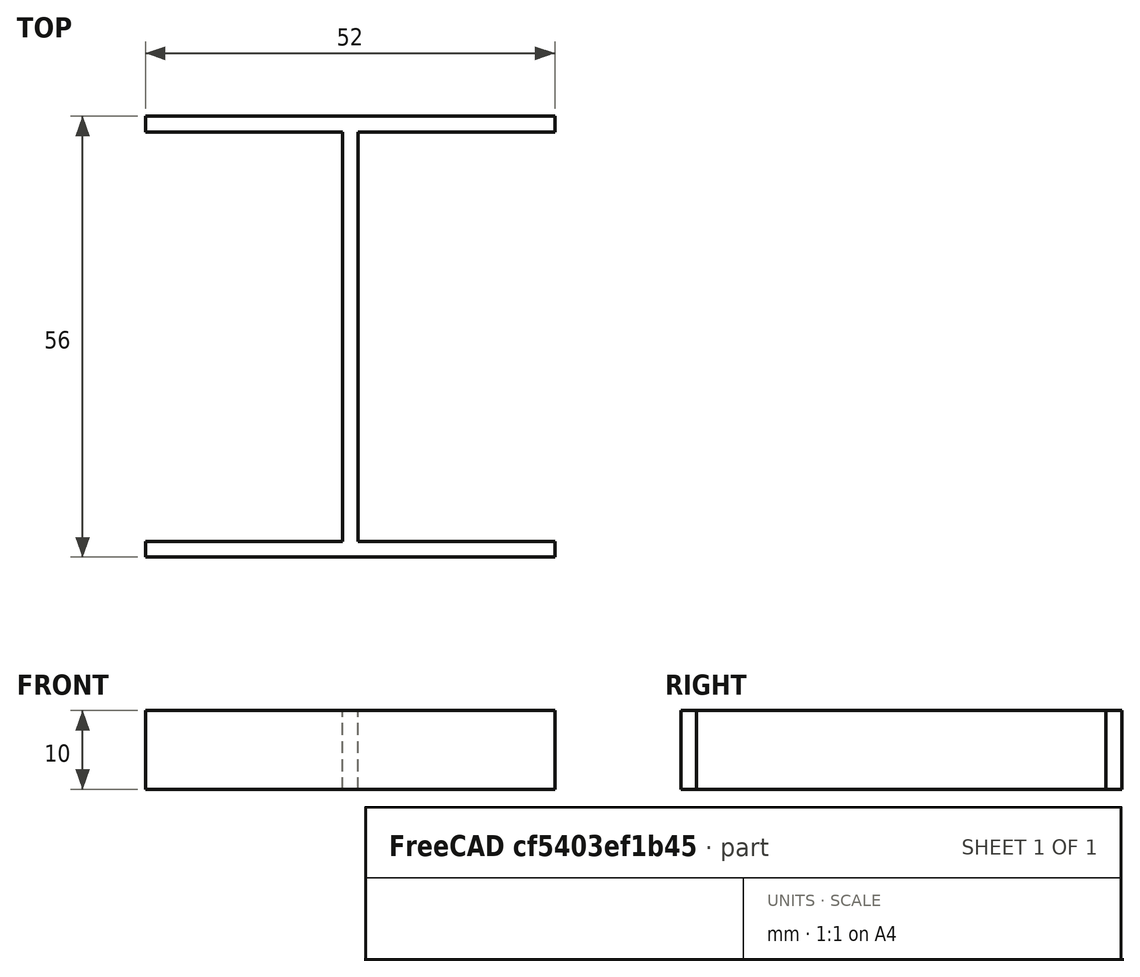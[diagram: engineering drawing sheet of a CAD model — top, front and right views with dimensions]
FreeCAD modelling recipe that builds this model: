
FCSTD DOCUMENT  (FreeCAD 1.0R38806 (Git))
Label: BedBracket
License: All rights reserved
LicenseURL: https://en.wikipedia.org/wiki/All_rights_reserved
objects: Sketcher::SketchObject×1, PartDesign::Pad×1, PartDesign::Body×1
note: 6 computed .brp shape members not serialized (recipe doc carries the construction recipe); baked Part::Feature solids carry a one-line shape summary decoded from their .brp

FEATURE [Sketcher::SketchObject] Sketch
  ArcFitTolerance = 1e-06
  AttachmentSupport = -> [XY_Plane]
  FullyConstrained = true
  MakeInternals = false
  MapMode = 5
  sketch-geometry (12):
    g0: LineSegment StartX=25 StartY=54 StartZ=0 EndX=25 EndY=2 EndZ=0
    g1: LineSegment StartX=25 StartY=2 StartZ=0 EndX=0 EndY=2 EndZ=0
    g2: LineSegment StartX=0 StartY=2 StartZ=0 EndX=0 EndY=0 EndZ=0
    g3: LineSegment StartX=0 StartY=0 StartZ=0 EndX=52 EndY=0 EndZ=0
    g4: LineSegment StartX=52 StartY=0 StartZ=0 EndX=52 EndY=2 EndZ=0
    g5: LineSegment StartX=52 StartY=2 StartZ=0 EndX=27 EndY=2 EndZ=0
    g6: LineSegment StartX=27 StartY=2 StartZ=0 EndX=27 EndY=54 EndZ=0
    g7: LineSegment StartX=27 StartY=54 StartZ=0 EndX=52 EndY=54 EndZ=0
    g8: LineSegment StartX=52 StartY=54 StartZ=0 EndX=52 EndY=56 EndZ=0
    g9: LineSegment StartX=52 StartY=56 StartZ=0 EndX=0 EndY=56 EndZ=0
    g10: LineSegment StartX=0 StartY=56 StartZ=0 EndX=0 EndY=54 EndZ=0
    g11: LineSegment StartX=0 StartY=54 StartZ=0 EndX=25 EndY=54 EndZ=0
  constraints (35):
    c: Vertical(g0)
    c: Coincident(g0,g1)
    c: Horizontal(g1)
    c: Coincident(g1,g2)
    c: Vertical(g2)
    c: Coincident(g2,g3)
    c: Horizontal(g3)
    c: Coincident(g3,g4)
    c: Vertical(g4)
    c: Coincident(g4,g5)
    c: Horizontal(g5)
    c: Coincident(g5,g6)
    c: Vertical(g6)
    c: Coincident(g6,g7)
    c: Horizontal(g7)
    c: Coincident(g7,g8)
    c: Vertical(g8)
    c: Coincident(g8,g9)
    c: Horizontal(g9)
    c: Coincident(g9,g10)
    c: Vertical(g10)
    c: Coincident(g10,g11)
    c: Coincident(g11,g0)
    c: Horizontal(g11)
    c: Horizontal(g11,g6)
    c: Horizontal(g1,g5)
    c: Vertical(g2,g10)
    c: Vertical(g5,g7)
    c: DistanceY(g0,g0) = 52
    c: Distance(g11,g11) = 25
    c: DistanceX(g7,g7) = 25
    c: DistanceY(g8,g8) = 2
    c: DistanceY(g4,g4) = 2
    c: Coincident(g2,g-1)
    c: Distance(g6,g0) = 2
FEATURE [PartDesign::Pad] Pad
  Direction = (0,0,1)
  Length = 10
  Length2 = 10
  Profile = -> Sketch
  ReferenceAxis = -> Sketch [N_Axis]
  Refine = true
  Suppressed = false
  Type = 0
FEATURE [PartDesign::Body] Body
  AllowCompound = false
  Group = -> [Sketch,Pad]
  Origin = -> Origin
  Tip = -> Pad
